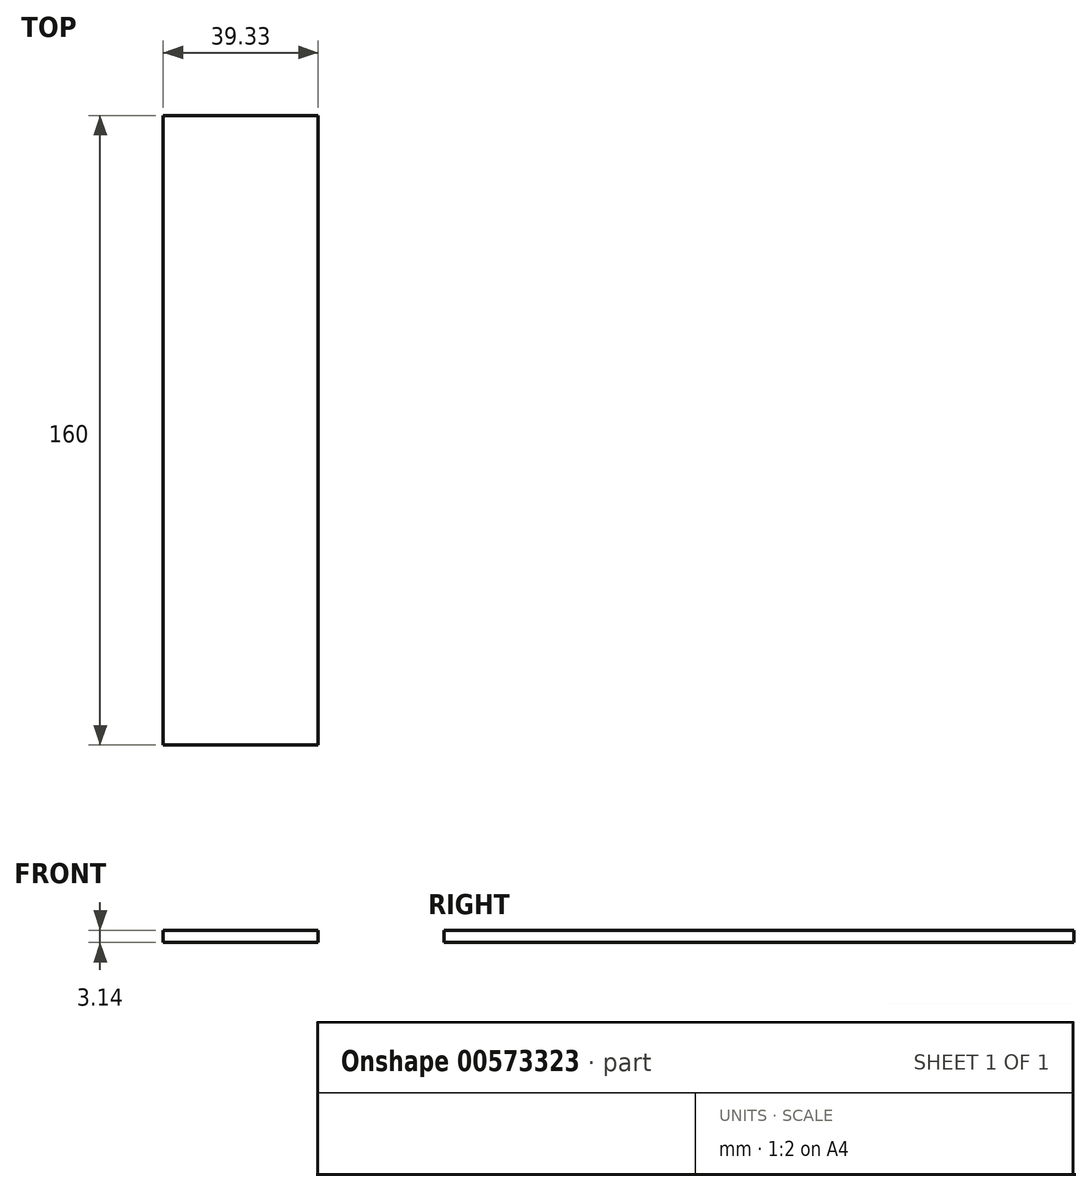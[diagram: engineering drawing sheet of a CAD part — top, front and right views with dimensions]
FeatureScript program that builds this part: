
annotation { "Feature Type Name" : "Feature", "Feature Type Description" : "" }
export const myFeature = defineFeature(function(context is Context, id is Id, definition is map)
    precondition{}
    {
        {
            var Q0;
            Q0=qCreatedBy(makeId("Top.planeOp"),FACE);
            var sketch = newSketch(context, id + "F0", { "sketchPlane" : qUnion([Q0])});
            skLineSegment(sketch, "E0.bottom", {"start": v(-16.92, 144.04) * mm, "end": v(22.4, 144.04) * mm});
            skLineSegment(sketch, "E0.top", {"start": v(-16.92, -15.96) * mm, "end": v(22.4, -15.96) * mm});
            skLineSegment(sketch, "E0.left", {"start": v(-16.92, 144.04) * mm, "end": v(-16.92, -15.96) * mm});
            skLineSegment(sketch, "E0.right", {"start": v(22.4, 144.04) * mm, "end": v(22.4, -15.96) * mm});
            skSolve(sketch);
        }
        {
            var Q0;
            Q0 = qSketchRegion(id + "F0", true);
            extrude(context, id + "F1", {"entities" : qUnion([Q0]), "depth" : 3.14 * mm, "offsetDistance" : 25 * mm});
        }
    });
